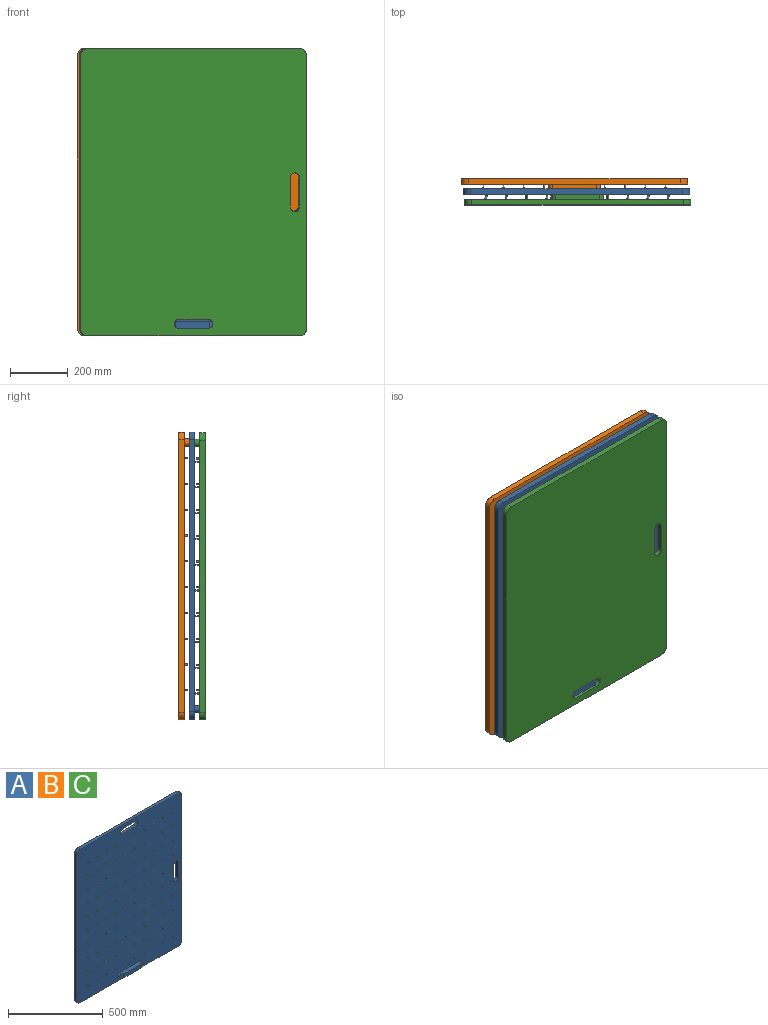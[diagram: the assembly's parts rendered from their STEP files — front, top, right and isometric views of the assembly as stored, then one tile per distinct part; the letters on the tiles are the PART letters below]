
ASSEMBLY  parts=3 mates=1
PART A: 227 faces, bbox 781.1x44.5x990.6 mm
  f0: plane 152.4x25.4mm, normal (0,0,-1), area 3671.4mm2, adj f2,f19,f221,f222,f223,f224,f225,f226
  f1: plane 152.4x25.4mm, normal (0,0,1), area 3671.4mm2, adj f2,f19,f221,f222,f223,f224,f225,f226
  f2: plane 115.48x25.4mm, normal (0,-1,0), area 2933.2mm2, adj f0,f1,f224,f226
  f3: plane 730.25x19.05mm, normal (0,0,-1), area 13911.3mm2, adj f4,f18,f19,f20
  f4: cylinder r=25.4mm len=25.4mm, axis (0,1,0), area 760.1mm2, adj f3,f5,f19,f20
  f5: plane 939.8x19.05mm, normal (1,0,0), area 17903.2mm2, adj f4,f6,f19,f20
  f6: cylinder r=25.4mm len=25.4mm, axis (0,1,0), area 760.1mm2, adj f5,f7,f19,f20
  f7: plane 730.25x19.05mm, normal (0,0,1), area 13911.3mm2, adj f6,f8,f19,f20
  f8: cylinder r=25.4mm len=25.4mm, axis (0,1,0), area 760.1mm2, adj f7,f9,f19,f20
  f9: plane 939.8x19.05mm, normal (-1,0,0), area 17903.2mm2, adj f8,f18,f19,f20
  f10: plane 101.6x19.05mm, normal (-1,0,0), area 1935.5mm2, adj f11,f16,f19,f20
  f11: cylinder r=15.88mm len=31.75mm, axis (0,1,0), area 950.1mm2, adj f10,f12,f19,f20
  f12: plane 101.6x19.05mm, normal (1,0,0), area 1935.5mm2, adj f11,f16,f19,f20
  f13: plane 101.6x19.05mm, normal (0,0,-1), area 1935.5mm2, adj f14,f17,f19,f20
  f14: cylinder r=15.88mm len=31.75mm, axis (0,1,0), area 950.1mm2, adj f13,f15,f19,f20
  f15: plane 101.6x19.05mm, normal (0,0,1), area 1935.5mm2, adj f14,f17,f19,f20
  f16: cylinder r=15.88mm len=31.75mm, axis (0,1,0), area 950.1mm2, adj f10,f12,f19,f20
  f17: cylinder r=15.88mm len=31.75mm, axis (0,1,0), area 950.1mm2, adj f13,f15,f19,f20
  f18: cylinder r=25.4mm len=25.4mm, axis (0,1,0), area 760.1mm2, adj f3,f9,f19,f20
  f19: plane 990.6x781.05mm, normal (0,-1,0), area 759457.4mm2, adj f0,f1,f3,f4,f5,f6,f7,f8
  f20: plane 990.6x781.05mm, normal (0,1,0), area 765119.3mm2, adj f3,f4,f5,f6,f7,f8,f9,f10
  f21: cylinder r=2.02mm len=12.7mm, axis (0,1,0), area 161.3mm2, adj f19,f22
  f22: plane 4.04x4.04mm, normal (0,-1,0), area 12.8mm2, adj f21
  f23: cylinder r=2.02mm len=12.7mm, axis (0,1,0), area 161.3mm2, adj f19,f24
  f24: plane 4.04x4.04mm, normal (0,-1,0), area 12.8mm2, adj f23
  f25: cylinder r=2.02mm len=12.7mm, axis (0,1,0), area 161.3mm2, adj f19,f26
  f26: plane 4.04x4.04mm, normal (0,-1,0), area 12.8mm2, adj f25
  f27: cylinder r=2.02mm len=12.7mm, axis (0,1,0), area 161.3mm2, adj f19,f28
  f28: plane 4.04x4.04mm, normal (0,-1,0), area 12.8mm2, adj f27
  f29: cylinder r=2.02mm len=12.7mm, axis (0,1,0), area 161.3mm2, adj f19,f30
  f30: plane 4.04x4.04mm, normal (0,-1,0), area 12.8mm2, adj f29
  f31: cylinder r=2.02mm len=12.7mm, axis (0,1,0), area 161.3mm2, adj f19,f32
  f32: plane 4.04x4.04mm, normal (0,-1,0), area 12.8mm2, adj f31
  f33: cylinder r=2.02mm len=12.7mm, axis (0,1,0), area 161.3mm2, adj f19,f34
  f34: plane 4.04x4.04mm, normal (0,-1,0), area 12.8mm2, adj f33
  f35: cylinder r=2.02mm len=12.7mm, axis (0,1,0), area 161.3mm2, adj f19,f36
  f36: plane 4.04x4.04mm, normal (0,-1,0), area 12.8mm2, adj f35
  f37: cylinder r=2.02mm len=12.7mm, axis (0,1,0), area 161.3mm2, adj f19,f38
  f38: plane 4.04x4.04mm, normal (0,-1,0), area 12.8mm2, adj f37
  f39: cylinder r=2.02mm len=12.7mm, axis (0,1,0), area 161.3mm2, adj f19,f40
  f40: plane 4.04x4.04mm, normal (0,-1,0), area 12.8mm2, adj f39
  f41: cylinder r=2.02mm len=12.7mm, axis (0,1,0), area 161.3mm2, adj f19,f42
  f42: plane 4.04x4.04mm, normal (0,-1,0), area 12.8mm2, adj f41
  f43: cylinder r=2.02mm len=12.7mm, axis (0,1,0), area 161.3mm2, adj f19,f44
  f44: plane 4.04x4.04mm, normal (0,-1,0), area 12.8mm2, adj f43
  f45: cylinder r=2.02mm len=12.7mm, axis (0,1,0), area 161.3mm2, adj f19,f46
  f46: plane 4.04x4.04mm, normal (0,-1,0), area 12.8mm2, adj f45
  f47: cylinder r=2.02mm len=12.7mm, axis (0,1,0), area 161.3mm2, adj f19,f48
  f48: plane 4.04x4.04mm, normal (0,-1,0), area 12.8mm2, adj f47
  f49: cylinder r=2.02mm len=12.7mm, axis (0,1,0), area 161.3mm2, adj f19,f50
  f50: plane 4.04x4.04mm, normal (0,-1,0), area 12.8mm2, adj f49
  f51: cylinder r=2.02mm len=12.7mm, axis (0,1,0), area 161.3mm2, adj f19,f52
  f52: plane 4.04x4.04mm, normal (0,-1,0), area 12.8mm2, adj f51
  f53: cylinder r=2.02mm len=12.7mm, axis (0,1,0), area 161.3mm2, adj f19,f54
  f54: plane 4.04x4.04mm, normal (0,-1,0), area 12.8mm2, adj f53
  f55: cylinder r=2.02mm len=12.7mm, axis (0,1,0), area 161.3mm2, adj f19,f56
  f56: plane 4.04x4.04mm, normal (0,-1,0), area 12.8mm2, adj f55
  f57: cylinder r=2.02mm len=12.7mm, axis (0,1,0), area 161.3mm2, adj f19,f58
  f58: plane 4.04x4.04mm, normal (0,-1,0), area 12.8mm2, adj f57
  f59: cylinder r=2.02mm len=12.7mm, axis (0,1,0), area 161.3mm2, adj f19,f60
  f60: plane 4.04x4.04mm, normal (0,-1,0), area 12.8mm2, adj f59
  f61: cylinder r=2.02mm len=12.7mm, axis (0,1,0), area 161.3mm2, adj f19,f62
  f62: plane 4.04x4.04mm, normal (0,-1,0), area 12.8mm2, adj f61
  f63: cylinder r=2.02mm len=12.7mm, axis (0,1,0), area 161.3mm2, adj f19,f64
  f64: plane 4.04x4.04mm, normal (0,-1,0), area 12.8mm2, adj f63
  f65: cylinder r=2.02mm len=12.7mm, axis (0,1,0), area 161.3mm2, adj f19,f66
  f66: plane 4.04x4.04mm, normal (0,-1,0), area 12.8mm2, adj f65
  f67: cylinder r=2.02mm len=12.7mm, axis (0,1,0), area 161.3mm2, adj f19,f68
  f68: plane 4.04x4.04mm, normal (0,-1,0), area 12.8mm2, adj f67
  f69: cylinder r=2.02mm len=12.7mm, axis (0,1,0), area 161.3mm2, adj f19,f70
  f70: plane 4.04x4.04mm, normal (0,-1,0), area 12.8mm2, adj f69
  f71: cylinder r=2.02mm len=12.7mm, axis (0,1,0), area 161.3mm2, adj f19,f72
  f72: plane 4.04x4.04mm, normal (0,-1,0), area 12.8mm2, adj f71
  f73: cylinder r=2.02mm len=12.7mm, axis (0,1,0), area 161.3mm2, adj f19,f74
  f74: plane 4.04x4.04mm, normal (0,-1,0), area 12.8mm2, adj f73
  f75: cylinder r=2.02mm len=12.7mm, axis (0,1,0), area 161.3mm2, adj f19,f76
  f76: plane 4.04x4.04mm, normal (0,-1,0), area 12.8mm2, adj f75
  f77: cylinder r=2.02mm len=12.7mm, axis (0,1,0), area 161.3mm2, adj f19,f78
  f78: plane 4.04x4.04mm, normal (0,-1,0), area 12.8mm2, adj f77
  f79: cylinder r=2.02mm len=12.7mm, axis (0,1,0), area 161.3mm2, adj f19,f80
  f80: plane 4.04x4.04mm, normal (0,-1,0), area 12.8mm2, adj f79
  f81: cylinder r=2.02mm len=12.7mm, axis (0,1,0), area 161.3mm2, adj f19,f82
  f82: plane 4.04x4.04mm, normal (0,-1,0), area 12.8mm2, adj f81
  f83: cylinder r=2.02mm len=12.7mm, axis (0,1,0), area 161.3mm2, adj f19,f84
  f84: plane 4.04x4.04mm, normal (0,-1,0), area 12.8mm2, adj f83
  f85: cylinder r=2.02mm len=12.7mm, axis (0,1,0), area 161.3mm2, adj f19,f86
  f86: plane 4.04x4.04mm, normal (0,-1,0), area 12.8mm2, adj f85
  f87: cylinder r=2.02mm len=12.7mm, axis (0,1,0), area 161.3mm2, adj f19,f88
  f88: plane 4.04x4.04mm, normal (0,-1,0), area 12.8mm2, adj f87
  f89: cylinder r=2.02mm len=12.7mm, axis (0,1,0), area 161.3mm2, adj f19,f90
  f90: plane 4.04x4.04mm, normal (0,-1,0), area 12.8mm2, adj f89
  f91: cylinder r=2.02mm len=12.7mm, axis (0,1,0), area 161.3mm2, adj f19,f92
  f92: plane 4.04x4.04mm, normal (0,-1,0), area 12.8mm2, adj f91
  f93: cylinder r=2.02mm len=12.7mm, axis (0,1,0), area 161.3mm2, adj f19,f94
  f94: plane 4.04x4.04mm, normal (0,-1,0), area 12.8mm2, adj f93
  f95: cylinder r=2.02mm len=12.7mm, axis (0,1,0), area 161.3mm2, adj f19,f96
  f96: plane 4.04x4.04mm, normal (0,-1,0), area 12.8mm2, adj f95
  f97: cylinder r=2.02mm len=12.7mm, axis (0,1,0), area 161.3mm2, adj f19,f98
  f98: plane 4.04x4.04mm, normal (0,-1,0), area 12.8mm2, adj f97
  f99: cylinder r=2.02mm len=12.7mm, axis (0,1,0), area 161.3mm2, adj f19,f100
  f100: plane 4.04x4.04mm, normal (0,-1,0), area 12.8mm2, adj f99
  f101: cylinder r=2.02mm len=12.7mm, axis (0,1,0), area 161.3mm2, adj f19,f102
  f102: plane 4.04x4.04mm, normal (0,-1,0), area 12.8mm2, adj f101
  f103: cylinder r=2.02mm len=12.7mm, axis (0,1,0), area 161.3mm2, adj f19,f104
  f104: plane 4.04x4.04mm, normal (0,-1,0), area 12.8mm2, adj f103
  f105: cylinder r=2.02mm len=12.7mm, axis (0,1,0), area 161.3mm2, adj f19,f106
  f106: plane 4.04x4.04mm, normal (0,-1,0), area 12.8mm2, adj f105
  f107: cylinder r=2.02mm len=12.7mm, axis (0,1,0), area 161.3mm2, adj f19,f108
  f108: plane 4.04x4.04mm, normal (0,-1,0), area 12.8mm2, adj f107
  f109: cylinder r=2.02mm len=12.7mm, axis (0,1,0), area 161.3mm2, adj f19,f110
  f110: plane 4.04x4.04mm, normal (0,-1,0), area 12.8mm2, adj f109
  f111: cylinder r=2.02mm len=12.7mm, axis (0,1,0), area 161.3mm2, adj f19,f112
  f112: plane 4.04x4.04mm, normal (0,-1,0), area 12.8mm2, adj f111
  f113: cylinder r=2.02mm len=12.7mm, axis (0,1,0), area 161.3mm2, adj f19,f114
  f114: plane 4.04x4.04mm, normal (0,-1,0), area 12.8mm2, adj f113
  f115: cylinder r=2.02mm len=12.7mm, axis (0,1,0), area 161.3mm2, adj f19,f116
  f116: plane 4.04x4.04mm, normal (0,-1,0), area 12.8mm2, adj f115
  f117: cylinder r=2.02mm len=12.7mm, axis (0,1,0), area 161.3mm2, adj f19,f118
  f118: plane 4.04x4.04mm, normal (0,-1,0), area 12.8mm2, adj f117
  f119: cylinder r=2.02mm len=12.7mm, axis (0,1,0), area 161.3mm2, adj f19,f120
  f120: plane 4.04x4.04mm, normal (0,-1,0), area 12.8mm2, adj f119
  f121: cylinder r=2.02mm len=12.7mm, axis (0,1,0), area 161.3mm2, adj f19,f122
  f122: plane 4.04x4.04mm, normal (0,-1,0), area 12.8mm2, adj f121
  f123: cylinder r=2.02mm len=12.7mm, axis (0,1,0), area 161.3mm2, adj f19,f124
  f124: plane 4.04x4.04mm, normal (0,-1,0), area 12.8mm2, adj f123
  f125: cylinder r=2.02mm len=12.7mm, axis (0,1,0), area 161.3mm2, adj f19,f126
  f126: plane 4.04x4.04mm, normal (0,-1,0), area 12.8mm2, adj f125
  f127: cylinder r=2.02mm len=12.7mm, axis (0,1,0), area 161.3mm2, adj f19,f128
  f128: plane 4.04x4.04mm, normal (0,-1,0), area 12.8mm2, adj f127
  f129: cylinder r=2.02mm len=12.7mm, axis (0,1,0), area 161.3mm2, adj f19,f130
  f130: plane 4.04x4.04mm, normal (0,-1,0), area 12.8mm2, adj f129
  f131: cylinder r=2.02mm len=12.7mm, axis (0,1,0), area 161.3mm2, adj f19,f132
  f132: plane 4.04x4.04mm, normal (0,-1,0), area 12.8mm2, adj f131
  f133: cylinder r=2.02mm len=12.7mm, axis (0,1,0), area 161.3mm2, adj f19,f134
  f134: plane 4.04x4.04mm, normal (0,-1,0), area 12.8mm2, adj f133
  f135: cylinder r=2.02mm len=12.7mm, axis (0,1,0), area 161.3mm2, adj f19,f136
  f136: plane 4.04x4.04mm, normal (0,-1,0), area 12.8mm2, adj f135
  f137: cylinder r=2.02mm len=12.7mm, axis (0,1,0), area 161.3mm2, adj f19,f138
  f138: plane 4.04x4.04mm, normal (0,-1,0), area 12.8mm2, adj f137
  f139: cylinder r=2.02mm len=12.7mm, axis (0,1,0), area 161.3mm2, adj f19,f140
  f140: plane 4.04x4.04mm, normal (0,-1,0), area 12.8mm2, adj f139
  f141: cylinder r=2.02mm len=12.7mm, axis (0,1,0), area 161.3mm2, adj f19,f142
  f142: plane 4.04x4.04mm, normal (0,-1,0), area 12.8mm2, adj f141
  f143: cylinder r=2.02mm len=12.7mm, axis (0,1,0), area 161.3mm2, adj f19,f144
  f144: plane 4.04x4.04mm, normal (0,-1,0), area 12.8mm2, adj f143
  f145: cylinder r=2.02mm len=12.7mm, axis (0,1,0), area 161.3mm2, adj f19,f146
  f146: plane 4.04x4.04mm, normal (0,-1,0), area 12.8mm2, adj f145
  f147: cylinder r=2.02mm len=12.7mm, axis (0,1,0), area 161.3mm2, adj f19,f148
  f148: plane 4.04x4.04mm, normal (0,-1,0), area 12.8mm2, adj f147
  f149: cylinder r=2.02mm len=12.7mm, axis (0,1,0), area 161.3mm2, adj f19,f150
  f150: plane 4.04x4.04mm, normal (0,-1,0), area 12.8mm2, adj f149
  f151: cylinder r=2.02mm len=12.7mm, axis (0,1,0), area 161.3mm2, adj f19,f152
  f152: plane 4.04x4.04mm, normal (0,-1,0), area 12.8mm2, adj f151
  f153: cylinder r=2.02mm len=12.7mm, axis (0,1,0), area 161.3mm2, adj f19,f154
  f154: plane 4.04x4.04mm, normal (0,-1,0), area 12.8mm2, adj f153
  f155: cylinder r=2.02mm len=12.7mm, axis (0,1,0), area 161.3mm2, adj f19,f156
  f156: plane 4.04x4.04mm, normal (0,-1,0), area 12.8mm2, adj f155
  f157: cylinder r=2.02mm len=12.7mm, axis (0,1,0), area 161.3mm2, adj f19,f158
  f158: plane 4.04x4.04mm, normal (0,-1,0), area 12.8mm2, adj f157
  f159: cylinder r=2.02mm len=12.7mm, axis (0,1,0), area 161.3mm2, adj f19,f160
  f160: plane 4.04x4.04mm, normal (0,-1,0), area 12.8mm2, adj f159
  f161: cylinder r=2.02mm len=12.7mm, axis (0,1,0), area 161.3mm2, adj f19,f162
  f162: plane 4.04x4.04mm, normal (0,-1,0), area 12.8mm2, adj f161
  f163: cylinder r=2.02mm len=12.7mm, axis (0,1,0), area 161.3mm2, adj f19,f164
  f164: plane 4.04x4.04mm, normal (0,-1,0), area 12.8mm2, adj f163
  f165: cylinder r=2.02mm len=12.7mm, axis (0,1,0), area 161.3mm2, adj f19,f166
  f166: plane 4.04x4.04mm, normal (0,-1,0), area 12.8mm2, adj f165
  f167: cylinder r=2.02mm len=12.7mm, axis (0,1,0), area 161.3mm2, adj f19,f168
  f168: plane 4.04x4.04mm, normal (0,-1,0), area 12.8mm2, adj f167
  f169: cylinder r=2.02mm len=12.7mm, axis (0,1,0), area 161.3mm2, adj f19,f170
  f170: plane 4.04x4.04mm, normal (0,-1,0), area 12.8mm2, adj f169
  f171: cylinder r=2.02mm len=12.7mm, axis (0,1,0), area 161.3mm2, adj f19,f172
  f172: plane 4.04x4.04mm, normal (0,-1,0), area 12.8mm2, adj f171
  f173: cylinder r=2.02mm len=12.7mm, axis (0,1,0), area 161.3mm2, adj f19,f174
  f174: plane 4.04x4.04mm, normal (0,-1,0), area 12.8mm2, adj f173
  f175: cylinder r=2.02mm len=12.7mm, axis (0,1,0), area 161.3mm2, adj f19,f176
  f176: plane 4.04x4.04mm, normal (0,-1,0), area 12.8mm2, adj f175
  f177: cylinder r=2.02mm len=12.7mm, axis (0,1,0), area 161.3mm2, adj f19,f178
  f178: plane 4.04x4.04mm, normal (0,-1,0), area 12.8mm2, adj f177
  f179: cylinder r=2.02mm len=12.7mm, axis (0,1,0), area 161.3mm2, adj f19,f180
  f180: plane 4.04x4.04mm, normal (0,-1,0), area 12.8mm2, adj f179
  f181: cylinder r=2.02mm len=12.7mm, axis (0,1,0), area 161.3mm2, adj f19,f182
  f182: plane 4.04x4.04mm, normal (0,-1,0), area 12.8mm2, adj f181
  f183: cylinder r=2.02mm len=12.7mm, axis (0,1,0), area 161.3mm2, adj f19,f184
  f184: plane 4.04x4.04mm, normal (0,-1,0), area 12.8mm2, adj f183
  f185: cylinder r=2.02mm len=12.7mm, axis (0,1,0), area 161.3mm2, adj f19,f186
  f186: plane 4.04x4.04mm, normal (0,-1,0), area 12.8mm2, adj f185
  f187: cylinder r=2.02mm len=12.7mm, axis (0,1,0), area 161.3mm2, adj f19,f188
  f188: plane 4.04x4.04mm, normal (0,-1,0), area 12.8mm2, adj f187
  f189: cylinder r=2.02mm len=12.7mm, axis (0,1,0), area 161.3mm2, adj f19,f190
  f190: plane 4.04x4.04mm, normal (0,-1,0), area 12.8mm2, adj f189
  f191: cylinder r=2.02mm len=12.7mm, axis (0,1,0), area 161.3mm2, adj f19,f192
  f192: plane 4.04x4.04mm, normal (0,-1,0), area 12.8mm2, adj f191
  f193: cylinder r=2.02mm len=12.7mm, axis (0,1,0), area 161.3mm2, adj f19,f194
  f194: plane 4.04x4.04mm, normal (0,-1,0), area 12.8mm2, adj f193
  f195: cylinder r=2.02mm len=12.7mm, axis (0,1,0), area 161.3mm2, adj f19,f196
  f196: plane 4.04x4.04mm, normal (0,-1,0), area 12.8mm2, adj f195
  f197: cylinder r=2.02mm len=12.7mm, axis (0,1,0), area 161.3mm2, adj f19,f198
  f198: plane 4.04x4.04mm, normal (0,-1,0), area 12.8mm2, adj f197
  f199: cylinder r=2.02mm len=12.7mm, axis (0,1,0), area 161.3mm2, adj f19,f200
  f200: plane 4.04x4.04mm, normal (0,-1,0), area 12.8mm2, adj f199
  f201: cylinder r=2.02mm len=12.7mm, axis (0,1,0), area 161.3mm2, adj f19,f202
  f202: plane 4.04x4.04mm, normal (0,-1,0), area 12.8mm2, adj f201
  f203: cylinder r=2.02mm len=12.7mm, axis (0,1,0), area 161.3mm2, adj f19,f204
  f204: plane 4.04x4.04mm, normal (0,-1,0), area 12.8mm2, adj f203
  f205: cylinder r=2.02mm len=12.7mm, axis (0,1,0), area 161.3mm2, adj f19,f206
  f206: plane 4.04x4.04mm, normal (0,-1,0), area 12.8mm2, adj f205
  f207: cylinder r=2.02mm len=12.7mm, axis (0,1,0), area 161.3mm2, adj f19,f208
  f208: plane 4.04x4.04mm, normal (0,-1,0), area 12.8mm2, adj f207
  f209: cylinder r=2.02mm len=12.7mm, axis (0,1,0), area 161.3mm2, adj f19,f210
  f210: plane 4.04x4.04mm, normal (0,-1,0), area 12.8mm2, adj f209
  f211: cylinder r=2.02mm len=12.7mm, axis (0,1,0), area 161.3mm2, adj f19,f212
  f212: plane 4.04x4.04mm, normal (0,-1,0), area 12.8mm2, adj f211
  f213: cylinder r=2.02mm len=12.7mm, axis (0,1,0), area 161.3mm2, adj f19,f214
  f214: plane 4.04x4.04mm, normal (0,-1,0), area 12.8mm2, adj f213
  f215: cylinder r=2.02mm len=12.7mm, axis (0,1,0), area 161.3mm2, adj f19,f216
  f216: plane 4.04x4.04mm, normal (0,-1,0), area 12.8mm2, adj f215
  f217: cylinder r=2.02mm len=12.7mm, axis (0,1,0), area 161.3mm2, adj f19,f218
  f218: plane 4.04x4.04mm, normal (0,-1,0), area 12.8mm2, adj f217
  f219: cylinder r=2.02mm len=12.7mm, axis (0,1,0), area 161.3mm2, adj f19,f220
  f220: plane 4.04x4.04mm, normal (0,-1,0), area 12.8mm2, adj f219
  f221: cylinder r=12.7mm len=25.4mm, axis (0,1,0), area 720.8mm2, adj f0,f1,f19,f225
  f222: cylinder r=12.7mm len=25.4mm, axis (0,1,0), area 741.9mm2, adj f0,f1,f19,f223
  f223: plane 25.4x22.15mm, normal (0,-1,0), area 493.5mm2, adj f0,f1,f222,f224
  f224: plane 25.4x8.96mm, normal (0.6,-0.8,0), area 285.9mm2, adj f0,f1,f2,f223
  f225: plane 25.4x22.77mm, normal (0,-1,0), area 509mm2, adj f0,f1,f221,f226
  f226: plane 25.4x8.44mm, normal (-0.66,-0.75,0), area 283.9mm2, adj f0,f1,f2,f225
PART B: same geometry as A
PART C: same geometry as A
PLACE A t=(-555.84,-285.27,-232.14)mm
PLACE B rot(axis=(0,-1,0),180deg) t=(-563.5,-249.35,-233.28)mm
PLACE C rot(axis=(1,0,0),180deg) t=(-552.34,-340.72,-234.05)mm fixed
MATE parallel A.f3 <-> B.f7  axis (0,0,-1) through (-555.84,-294.8,-727.44)mm
